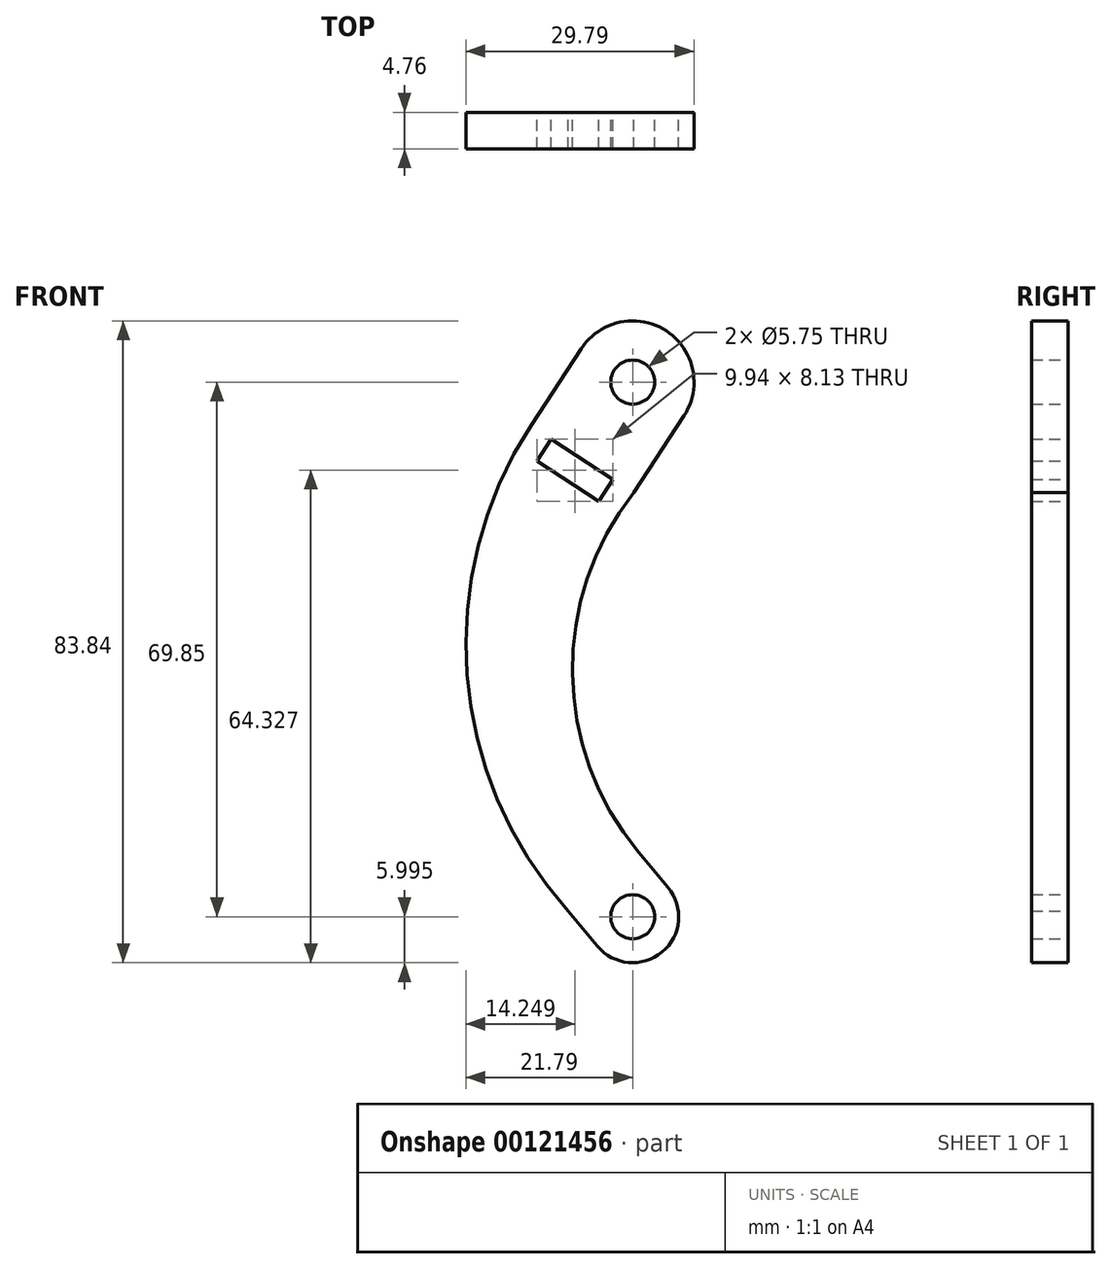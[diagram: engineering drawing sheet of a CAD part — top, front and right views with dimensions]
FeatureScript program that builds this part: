
annotation { "Feature Type Name" : "Feature", "Feature Type Description" : "" }
export const myFeature = defineFeature(function(context is Context, id is Id, definition is map)
    precondition{}
    {
        {
            var Q0;
            Q0=qCreatedBy(makeId("Front.planeOp"),FACE);
            var sketch = newSketch(context, id + "F0", { "sketchPlane" : qUnion([Q0])});
            skCircle(sketch, "E0", {"center": v(0, -34.93) * mm, "radius": 2.87 * mm});
            skArc(sketch, "E1", {"start": v(-4.61, -38.76) * mm, "mid": v(3.84, -39.54) * mm, "end": v(4.61, -31.09) * mm});
            skCircle(sketch, "E2", {"center": v(0, 34.93) * mm, "radius": 2.87 * mm});
            skArc(sketch, "E3", {"start": v(6.7, 30.54) * mm, "mid": v(4.38, 41.62) * mm, "end": v(-6.7, 39.3) * mm});
            skLineSegment(sketch, "E4", {"start": v(0, -34.93) * mm, "end": v(-4.18, -29.9) * mm, "construction": true});
            skLineSegment(sketch, "E5.0", {"start": v(-4.61, -38.76) * mm, "end": v(-8.45, -34.15) * mm});
            skLineSegment(sketch, "E6.MirrorCS", {"start": v(4.61, -31.09) * mm, "end": v(0.77, -26.47) * mm});
            skLineSegment(sketch, "E7", {"start": v(0, 34.92) * mm, "end": v(-8.47, 21.98) * mm, "construction": true});
            skLineSegment(sketch, "E8.0", {"start": v(-6.7, 39.3) * mm, "end": v(-13.27, 29.27) * mm});
            skLineSegment(sketch, "E9.MirrorCS", {"start": v(6.7, 30.54) * mm, "end": v(0.12, 20.5) * mm});
            skArc(sketch, "E10", {"start": v(0.12, 20.5) * mm, "mid": v(-7.87, -3.1) * mm, "end": v(0.77, -26.47) * mm});
            skArc(sketch, "E11", {"start": v(-13.27, 29.27) * mm, "mid": v(-21.64, -3.26) * mm, "end": v(-8.45, -34.15) * mm});
            skLineSegment(sketch, "E12", {"start": v(-21.78, 0) * mm, "end": v(-7.78, 0) * mm, "construction": true});
            skLineSegment(sketch, "E13", {"start": v(-10.65, 27.47) * mm, "end": v(-12.5, 24.63) * mm});
            skLineSegment(sketch, "E14", {"start": v(-12.5, 24.63) * mm, "end": v(-8.47, 21.98) * mm});
            skLineSegment(sketch, "E15", {"start": v(-10.65, 27.47) * mm, "end": v(-6.6, 24.83) * mm});
            skLineSegment(sketch, "E16.MirrorCS", {"start": v(-2.57, 22.19) * mm, "end": v(-6.6, 24.83) * mm});
            skLineSegment(sketch, "E17.MirrorCS", {"start": v(-2.57, 22.19) * mm, "end": v(-4.44, 19.34) * mm});
            skLineSegment(sketch, "E18.MirrorCS", {"start": v(-4.44, 19.34) * mm, "end": v(-8.47, 21.98) * mm});
            skSolve(sketch);
        }
        {
            var Q0;
            Q0=makeQuery(id+"F0.imprint","IMPRINT",FACE,{"disambiguationData":[TD([[makeQuery(id+"F0.imprint","IMPRINT",EDGE,{"derivedFrom":sQuery(id+"F0.wireOp",EDGE,"E0")}),-1.0]])]});
            extrude(context, id + "F1", {"entities" : qUnion([Q0]), "depth" : 4.76 * mm});
        }
    });
